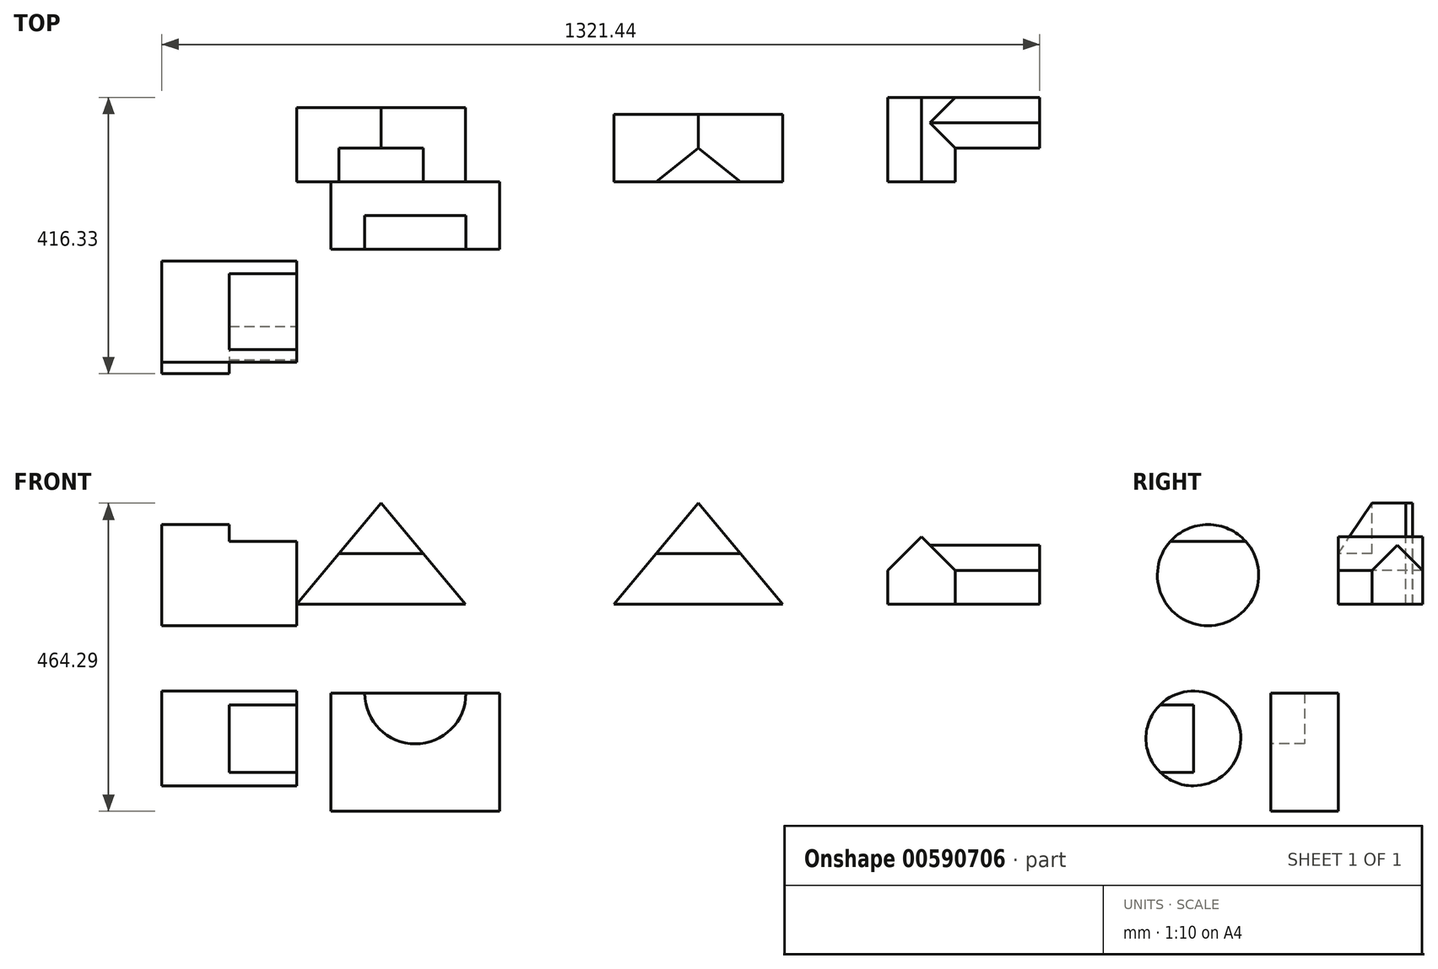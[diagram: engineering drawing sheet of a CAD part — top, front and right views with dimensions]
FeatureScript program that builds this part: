
annotation { "Feature Type Name" : "Feature", "Feature Type Description" : "" }
export const myFeature = defineFeature(function(context is Context, id is Id, definition is map)
    precondition{}
    {
        {
            var Q0;
            Q0=qCreatedBy(makeId("Front.planeOp"),FACE);
            var sketch = newSketch(context, id + "F0", { "sketchPlane" : qUnion([Q0])});
            skLineSegment(sketch, "E0", {"start": v(0, 0) * mm, "end": v(254, 0) * mm});
            skLineSegment(sketch, "E1", {"start": v(254, 0) * mm, "end": v(127, 152.4) * mm});
            skLineSegment(sketch, "E2", {"start": v(127, 152.4) * mm, "end": v(0, 0) * mm});
            skSolve(sketch);
        }
        {
            var Q0;
            Q0=makeQuery(id+"F0.imprint","IMPRINT",FACE,{"disambiguationData":[TD([[makeQuery(id+"F0.imprint","IMPRINT",EDGE,{"derivedFrom":sQuery(id+"F0.wireOp",EDGE,"E0")}),1.0]])]});
            extrude(context, id + "F1", {"entities" : qUnion([Q0]), "oppositeDirection" : true, "depth" : 111.76 * mm, "offsetDistance" : 25.4 * mm});
        }
        {
            var Q0;
            Q0=makeQuery(id+"F1.opExtrude","CAP_FACE",FACE,{"disambiguationData":[OSD([sQuery(id+"F0.wireOp",EDGE,"E0"),sQuery(id+"F0.wireOp",EDGE,"E1"),sQuery(id+"F0.wireOp",EDGE,"E2")])],"isStart":true});
            var sketch = newSketch(context, id + "F2", { "sketchPlane" : qUnion([Q0])});
            skLineSegment(sketch, "E3", {"start": v(63.5, 76.2) * mm, "end": v(190.5, 76.2) * mm});
            skLineSegment(sketch, "E4", {"start": v(63.5, 76.2) * mm, "end": v(127, 152.4) * mm});
            skLineSegment(sketch, "E5", {"start": v(127, 152.4) * mm, "end": v(190.5, 76.2) * mm});
            skSolve(sketch);
        }
        {
            var Q0;
            Q0=makeQuery(id+"F2.imprint","IMPRINT",FACE,{"disambiguationData":[TD([[makeQuery(id+"F2.imprint","IMPRINT",EDGE,{"derivedFrom":sQuery(id+"F2.wireOp",EDGE,"E3")}),1.0]])]});
            extrude(context, id + "F3", {"entities" : qUnion([Q0]), "operationType" : NewBodyOperationType.REMOVE, "oppositeDirection" : true, "depth" : 50.8 * mm, "offsetDistance" : 25.4 * mm});
        }
        {
            var Q0;
            Q0=qCreatedBy(makeId("Front.planeOp"),FACE);
            var sketch = newSketch(context, id + "F4", { "sketchPlane" : qUnion([Q0])});
            skLineSegment(sketch, "E6", {"start": v(477.44, 0) * mm, "end": v(731.44, 0) * mm});
            skLineSegment(sketch, "E7", {"start": v(731.44, 0) * mm, "end": v(604.44, 152.4) * mm});
            skLineSegment(sketch, "E8", {"start": v(604.44, 152.4) * mm, "end": v(477.44, 0) * mm});
            skSolve(sketch);
        }
        {
            var Q0;
            Q0=makeQuery(id+"F4.imprint","IMPRINT",FACE,{"disambiguationData":[TD([[makeQuery(id+"F4.imprint","IMPRINT",EDGE,{"derivedFrom":sQuery(id+"F4.wireOp",EDGE,"E6")}),1.0]])]});
            extrude(context, id + "F5", {"entities" : qUnion([Q0]), "oppositeDirection" : true, "depth" : 101.6 * mm, "offsetDistance" : 25.4 * mm});
        }
        {
            var Q0;
            Q0=makeQuery(id+"F5.opExtrude","CAP_EDGE",EDGE,{"disambiguationData":[OSD([sQuery(id+"F4.wireOp",EDGE,"E6")])],"isStart":true});
            cPoint(context, id + "F6", {"entities" : qUnion([Q0]), "parameter" : 0.5});
        }
        {
            var Q0;
            Q0=makeQuery(id+"F5.opExtrude","CAP_VERTEX",VERTEX,{"disambiguationData":[OSD([sQuery(id+"F4.wireOp",EDGE,"E7"),sQuery(id+"F4.wireOp",EDGE,"E8")])],"isStart":true});
            var Q1;
            Q1=makeQuery(id+"F5.opExtrude","CAP_VERTEX",VERTEX,{"disambiguationData":[OSD([sQuery(id+"F4.wireOp",EDGE,"E7"),sQuery(id+"F4.wireOp",EDGE,"E8")])],"isStart":false});
            var Q2;
            Q2 = qCreatedBy(id + "F6" ,VERTEX);
            cPlane(context, id + "F7", {"entities" : qUnion([Q0, Q1, Q2]), "cplaneType" : CPlaneType.THREE_POINT, "offset" : 25.4 * mm, "width" : 152.4 * mm, "height" : 152.4 * mm});
        }
        {
            var Q0;
            Q0=qCreatedBy(id+"F7.planeOp",FACE);
            var sketch = newSketch(context, id + "F8", { "sketchPlane" : qUnion([Q0])});
            skLineSegment(sketch, "E9", {"start": v(0, 76.2) * mm, "end": v(50.8, 152.4) * mm});
            skLineSegment(sketch, "E10", {"start": v(50.8, 152.4) * mm, "end": v(0, 152.4) * mm});
            skLineSegment(sketch, "E11", {"start": v(0, 152.4) * mm, "end": v(0, 76.2) * mm});
            skSolve(sketch);
        }
        {
            var Q0;
            Q0 = qSketchRegion(id + "F8", true);
            extrude(context, id + "F9", {"entities" : qUnion([Q0]), "operationType" : NewBodyOperationType.REMOVE, "endBound" : BoundingType.SYMMETRIC, "oppositeDirection" : true, "depth" : 152.4 * mm, "offsetDistance" : 25.4 * mm});
        }
        {
            var Q0;
            Q0=qCreatedBy(makeId("Front.planeOp"),FACE);
            var sketch = newSketch(context, id + "F10", { "sketchPlane" : qUnion([Q0])});
            skLineSegment(sketch, "E12", {"start": v(889.64, 0) * mm, "end": v(991.24, 0) * mm});
            skLineSegment(sketch, "E13", {"start": v(991.24, 0) * mm, "end": v(991.24, 50.8) * mm});
            skLineSegment(sketch, "E14", {"start": v(991.24, 50.8) * mm, "end": v(940.44, 101.6) * mm});
            skLineSegment(sketch, "E15", {"start": v(940.44, 101.6) * mm, "end": v(889.64, 50.8) * mm});
            skLineSegment(sketch, "E16", {"start": v(889.64, 50.8) * mm, "end": v(889.64, 0) * mm});
            skSolve(sketch);
        }
        {
            var Q0;
            Q0=makeQuery(id+"F10.imprint","IMPRINT",FACE,{"disambiguationData":[TD([[makeQuery(id+"F10.imprint","IMPRINT",EDGE,{"derivedFrom":sQuery(id+"F10.wireOp",EDGE,"E12")}),1.0]])]});
            extrude(context, id + "F11", {"entities" : qUnion([Q0]), "oppositeDirection" : true, "depth" : 127 * mm, "offsetDistance" : 25.4 * mm});
        }
        {
            var Q0;
            Q0=makeQuery(id+"F11.opExtrude","SWEPT_FACE",FACE,{"disambiguationData":[OSD([sQuery(id+"F10.wireOp",EDGE,"E13")])]});
            cPlane(context, id + "F12", {"entities" : qUnion([Q0]), "cplaneType" : CPlaneType.OFFSET, "offset" : 127 * mm, "width" : 152.4 * mm, "height" : 152.4 * mm});
        }
        {
            var Q0;
            Q0=qCreatedBy(id+"F12.planeOp",FACE);
            var sketch = newSketch(context, id + "F13", { "sketchPlane" : qUnion([Q0])});
            skLineSegment(sketch, "E17", {"start": v(50.8, 0) * mm, "end": v(50.8, 50.8) * mm});
            skLineSegment(sketch, "E18", {"start": v(50.8, 50.8) * mm, "end": v(88.9, 88.9) * mm});
            skLineSegment(sketch, "E19", {"start": v(88.9, 88.9) * mm, "end": v(127, 50.8) * mm});
            skLineSegment(sketch, "E20", {"start": v(127, 50.8) * mm, "end": v(127, 0) * mm});
            skLineSegment(sketch, "E21", {"start": v(127, 0) * mm, "end": v(50.8, 0) * mm});
            skSolve(sketch);
        }
        {
            var Q0;
            Q0=makeQuery(id+"F13.imprint","IMPRINT",FACE,{"disambiguationData":[TD([[makeQuery(id+"F13.imprint","IMPRINT",EDGE,{"derivedFrom":sQuery(id+"F13.wireOp",EDGE,"E17")}),-1.0]])]});
            extrude(context, id + "F14", {"entities" : qUnion([Q0]), "operationType" : NewBodyOperationType.ADD, "endBound" : BoundingType.UP_TO_NEXT, "oppositeDirection" : true, "depth" : 152.4 * mm, "offsetDistance" : 25.4 * mm});
        }
        {
            var Q0;
            Q0=qCreatedBy(makeId("Right.planeOp"),FACE);
            var sketch = newSketch(context, id + "F15", { "sketchPlane" : qUnion([Q0])});
            skCircle(sketch, "E22", {"center": v(-195.9, 44) * mm, "radius": 76.2 * mm});
            skLineSegment(sketch, "E23", {"start": v(-195.9, 44) * mm, "end": v(-119.7, 44) * mm});
            skSolve(sketch);
        }
        {
            var Q0;
            Q0=makeQuery(id+"F15.imprint","IMPRINT",FACE,{"disambiguationData":[TD([[makeQuery(id+"F15.imprint","IMPRINT",EDGE,{"derivedFrom":sQuery(id+"F15.wireOp",EDGE,"E22")}),1.0]])]});
            extrude(context, id + "F16", {"entities" : qUnion([Q0]), "oppositeDirection" : true, "depth" : 203.2 * mm, "offsetDistance" : 25.4 * mm});
        }
        {
            var Q0;
            Q0=makeQuery(id+"F16.opExtrude","CAP_FACE",FACE,{"disambiguationData":[OSD([sQuery(id+"F15.wireOp",EDGE,"E22")])],"isStart":true});
            var sketch = newSketch(context, id + "F17", { "sketchPlane" : qUnion([Q0])});
            skLineSegment(sketch, "E24", {"start": v(-252.8, 94.7) * mm, "end": v(-139, 94.7) * mm});
            skLineSegment(sketch, "E25", {"start": v(-200.06, 94.7) * mm, "end": v(-200.06, 120.1) * mm});
            skSolve(sketch);
        }
        {
            var Q0;
            {var subQ3=sQuery(id+"F17.wireOp",EDGE,"E25");Q0=makeQuery(id+"F17.imprint","IMPRINT",FACE,{"disambiguationData":[TD([[makeQuery(id+"F17.imprint","IMPRINT",EDGE,{"derivedFrom":subQ3}),-1.0]])]});}
            var Q1;
            {var subQ3=sQuery(id+"F17.wireOp",EDGE,"E25");Q1=makeQuery(id+"F17.imprint","IMPRINT",FACE,{"disambiguationData":[TD([[makeQuery(id+"F17.imprint","IMPRINT",EDGE,{"derivedFrom":subQ3}),1.0]])]});}
            extrude(context, id + "F18", {"entities" : qUnion([Q0, Q1]), "operationType" : NewBodyOperationType.REMOVE, "oppositeDirection" : true, "depth" : 101.6 * mm, "offsetDistance" : 25.4 * mm});
        }
        {
            var Q0;
            Q0=qCreatedBy(makeId("Right.planeOp"),FACE);
            var sketch = newSketch(context, id + "F19", { "sketchPlane" : qUnion([Q0])});
            skCircle(sketch, "E26", {"center": v(-217.97, -202.07) * mm, "radius": 71.36 * mm});
            skSolve(sketch);
        }
        {
            var Q0;
            Q0=makeQuery(id+"F19.imprint","IMPRINT",FACE,{"disambiguationData":[TD([[makeQuery(id+"F19.imprint","IMPRINT",EDGE,{"derivedFrom":sQuery(id+"F19.wireOp",EDGE,"E26")}),1.0]])]});
            extrude(context, id + "F20", {"entities" : qUnion([Q0]), "oppositeDirection" : true, "depth" : 203.2 * mm, "offsetDistance" : 25.4 * mm});
        }
        {
            var Q0;
            Q0=makeQuery(id+"F20.opExtrude","CAP_FACE",FACE,{"disambiguationData":[OSD([sQuery(id+"F19.wireOp",EDGE,"E26")])],"isStart":true});
            var sketch = newSketch(context, id + "F21", { "sketchPlane" : qUnion([Q0])});
            skLineSegment(sketch, "E27", {"start": v(-217.97, -202.07) * mm, "end": v(-217.97, -151.27) * mm});
            skLineSegment(sketch, "E28", {"start": v(-217.97, -202.07) * mm, "end": v(-217.97, -252.87) * mm});
            skLineSegment(sketch, "E29", {"start": v(-217.97, -151.27) * mm, "end": v(-268.1, -151.27) * mm});
            skLineSegment(sketch, "E30", {"start": v(-217.97, -252.87) * mm, "end": v(-268.1, -252.87) * mm});
            skSolve(sketch);
        }
        {
            var Q0;
            Q0=makeQuery(id+"F21.imprint","IMPRINT",FACE,{"disambiguationData":[TD([[makeQuery(id+"F21.imprint","IMPRINT",EDGE,{"derivedFrom":sQuery(id+"F21.wireOp",EDGE,"E27")}),1.0]])]});
            extrude(context, id + "F22", {"entities" : qUnion([Q0]), "operationType" : NewBodyOperationType.REMOVE, "oppositeDirection" : true, "depth" : 101.6 * mm, "offsetDistance" : 25.4 * mm});
        }
        {
            var Q0;
            Q0=qCreatedBy(makeId("Front.planeOp"),FACE);
            var sketch = newSketch(context, id + "F23", { "sketchPlane" : qUnion([Q0])});
            skLineSegment(sketch, "E31", {"start": v(51.4, -134.1) * mm, "end": v(305.4, -134.1) * mm});
            skLineSegment(sketch, "E32", {"start": v(305.4, -134.1) * mm, "end": v(305.4, -311.9) * mm});
            skLineSegment(sketch, "E33", {"start": v(51.4, -134.1) * mm, "end": v(51.4, -311.9) * mm});
            skLineSegment(sketch, "E34", {"start": v(51.4, -311.9) * mm, "end": v(305.4, -311.9) * mm});
            skSolve(sketch);
        }
        {
            var Q0;
            Q0=makeQuery(id+"F23.imprint","IMPRINT",FACE,{"disambiguationData":[TD([[makeQuery(id+"F23.imprint","IMPRINT",EDGE,{"derivedFrom":sQuery(id+"F23.wireOp",EDGE,"E31")}),-1.0]])]});
            extrude(context, id + "F24", {"entities" : qUnion([Q0]), "depth" : 101.6 * mm, "offsetDistance" : 25.4 * mm});
        }
        {
            var Q0;
            Q0=makeQuery(id+"F24.opExtrude","CAP_FACE",FACE,{"disambiguationData":[OSD([sQuery(id+"F23.wireOp",EDGE,"E31"),sQuery(id+"F23.wireOp",EDGE,"E32"),sQuery(id+"F23.wireOp",EDGE,"E33"),sQuery(id+"F23.wireOp",EDGE,"E34")])],"isStart":false});
            var sketch = newSketch(context, id + "F25", { "sketchPlane" : qUnion([Q0])});
            skCircle(sketch, "E35", {"center": v(178.4, -134.1) * mm, "radius": 76.2 * mm});
            skSolve(sketch);
        }
        {
            var Q0;
            {var subQ0=sQuery(id+"F25.wireOp",EDGE,"E35");var subQ1=makeQuery(id+"F24.opExtrude","CAP_EDGE",EDGE,{"disambiguationData":[OSD([sQuery(id+"F23.wireOp",EDGE,"E31")])],"isStart":false});var subQ2=makeQuery(id+"F25.imprint","INTERSECT",VERTEX,{"disambiguationData":[OD(0.0)],"derivedFrom":[subQ1,subQ0]});Q0=makeQuery(id+"F25.imprint","IMPRINT",FACE,{"disambiguationData":[TD([[makeQuery(id+"F25.imprint","IMPRINT",EDGE,{"disambiguationData":[TD([[subQ2,1.0]])],"derivedFrom":subQ0}),1.0]])]});}
            var Q1;
            {var subQ0=sQuery(id+"F25.wireOp",EDGE,"E35");var subQ1=makeQuery(id+"F24.opExtrude","CAP_EDGE",EDGE,{"disambiguationData":[OSD([sQuery(id+"F23.wireOp",EDGE,"E31")])],"isStart":false});var subQ2=makeQuery(id+"F25.imprint","INTERSECT",VERTEX,{"disambiguationData":[OD(0.0)],"derivedFrom":[subQ1,subQ0]});Q1=makeQuery(id+"F25.imprint","IMPRINT",FACE,{"disambiguationData":[TD([[makeQuery(id+"F25.imprint","IMPRINT",EDGE,{"disambiguationData":[TD([[subQ2,-1.0]])],"derivedFrom":subQ0}),1.0]])]});}
            extrude(context, id + "F26", {"entities" : qUnion([Q0, Q1]), "operationType" : NewBodyOperationType.REMOVE, "oppositeDirection" : true, "depth" : 50.8 * mm, "offsetDistance" : 25.4 * mm});
        }
    });
